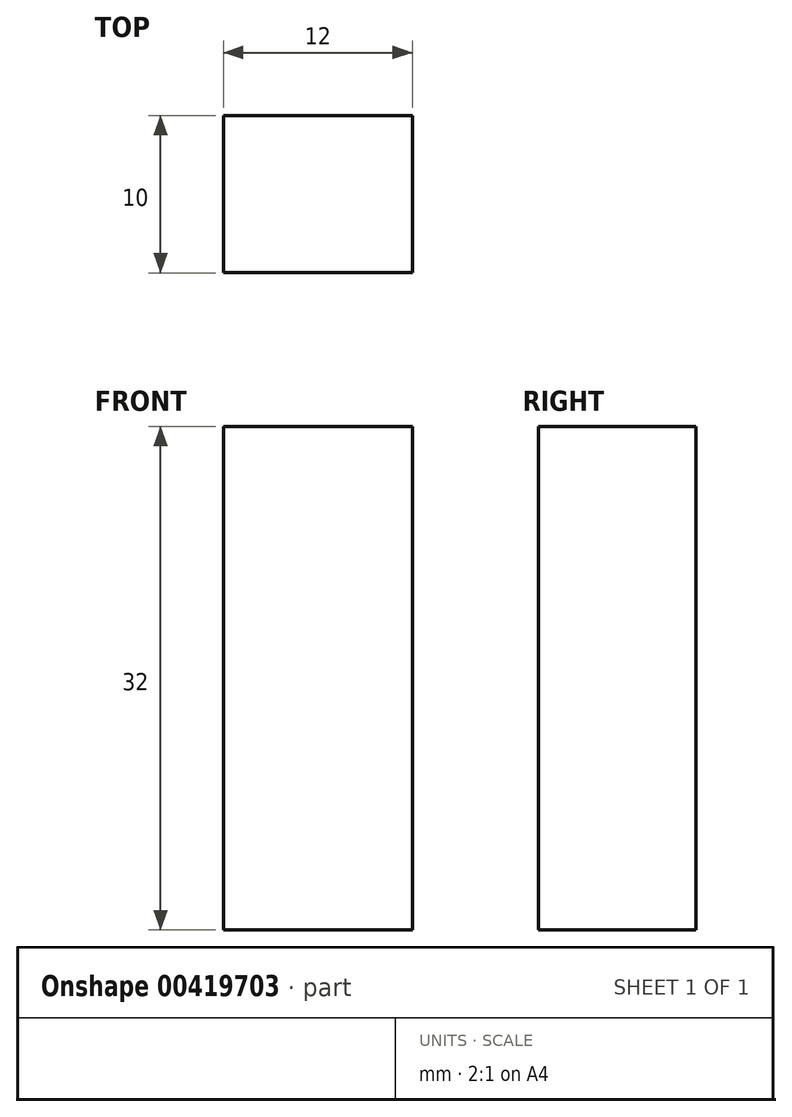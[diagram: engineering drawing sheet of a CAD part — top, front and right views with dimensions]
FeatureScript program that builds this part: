
annotation { "Feature Type Name" : "Feature", "Feature Type Description" : "" }
export const myFeature = defineFeature(function(context is Context, id is Id, definition is map)
    precondition{}
    {
        {
            var Q0;
            Q0=qCreatedBy(makeId("Top.planeOp"),FACE);
            var sketch = newSketch(context, id + "F0", { "sketchPlane" : qUnion([Q0])});
            skLineSegment(sketch, "E0.bottom", {"start": v(-12, 4.1) * mm, "end": v(0, 4.1) * mm});
            skLineSegment(sketch, "E0.top", {"start": v(-12, -5.9) * mm, "end": v(0, -5.9) * mm});
            skLineSegment(sketch, "E0.left", {"start": v(-12, 4.1) * mm, "end": v(-12, -5.9) * mm});
            skLineSegment(sketch, "E0.right", {"start": v(0, 4.1) * mm, "end": v(0, -5.9) * mm});
            skSolve(sketch);
        }
        {
            var Q0;
            Q0=makeQuery(id+"F0.imprint","IMPRINT",FACE,{"disambiguationData":[TD([[makeQuery(id+"F0.imprint","IMPRINT",EDGE,{"derivedFrom":sQuery(id+"F0.wireOp",EDGE,"E0.bottom")}),-1.0]])]});
            extrude(context, id + "F1", {"entities" : qUnion([Q0]), "depth" : 32 * mm});
        }
    });
